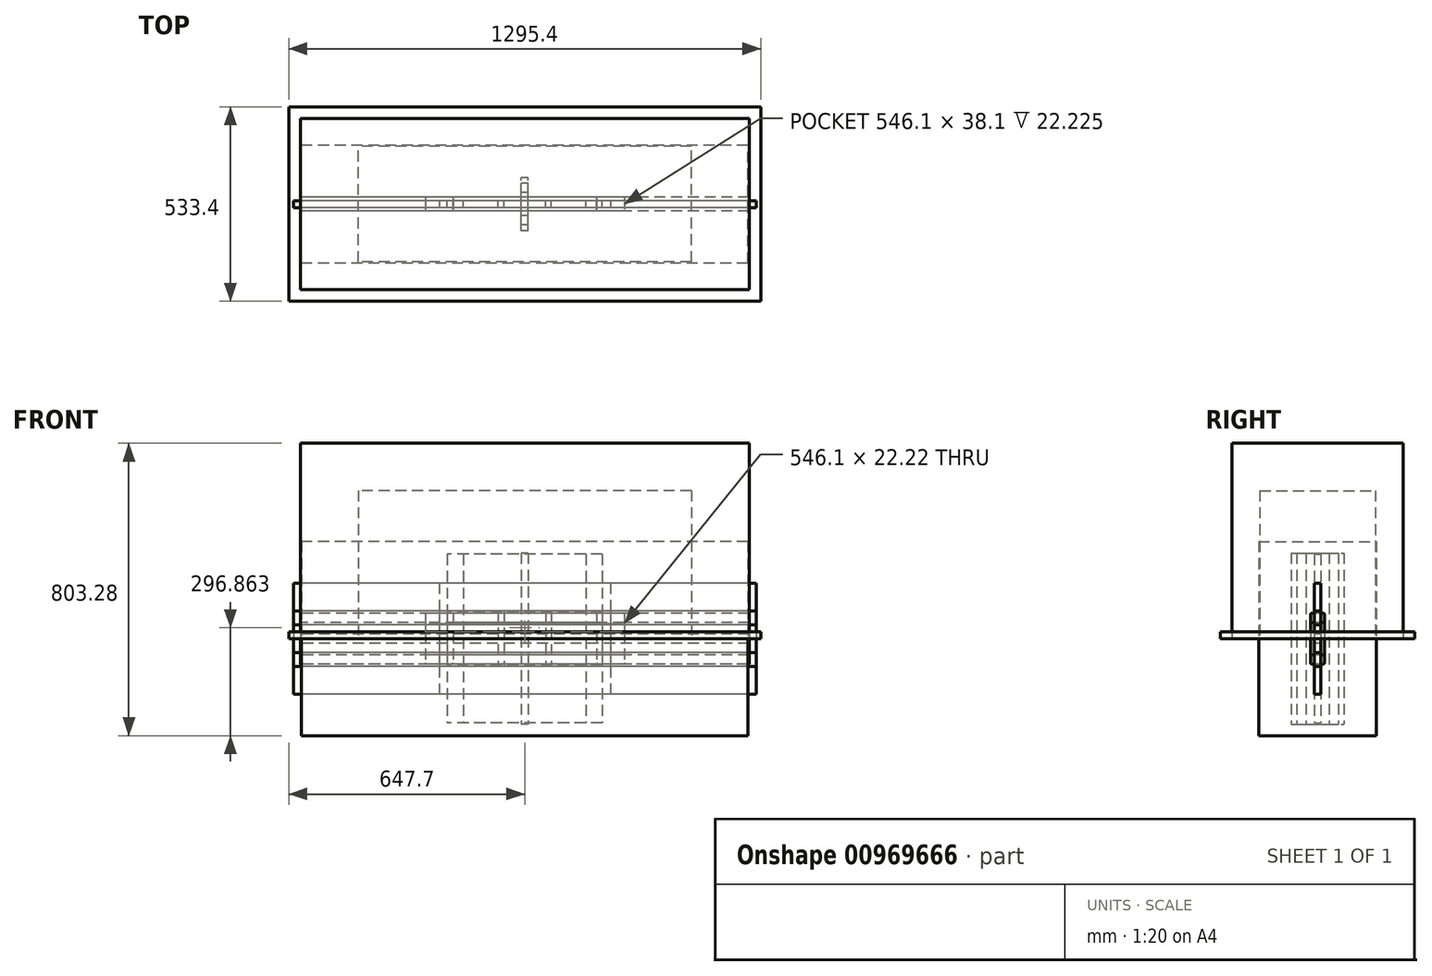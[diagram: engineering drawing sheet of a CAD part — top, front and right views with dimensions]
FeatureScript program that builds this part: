
annotation { "Feature Type Name" : "Feature", "Feature Type Description" : "" }
export const myFeature = defineFeature(function(context is Context, id is Id, definition is map)
    precondition{}
    {
        {
            assignVariable(context, id + "F0", {"name" : "TankLength", "anyValue" : 1231.9 * mm});
        }
        {
            assignVariable(context, id + "F1", {"name" : "TankHeight", "anyValue" : 536.57 * mm});
        }
        {
            assignVariable(context, id + "F2", {"name" : "TankWidth", "anyValue" : 469.9 * mm});
        }
        {
            assignVariable(context, id + "F3", {"name" : "SumpHeight", "lengthValue" : 406.4 * mm, "variableType" : VariableType.LENGTH});
        }
        {
            var Q0;
            Q0=qCreatedBy(makeId("Top.planeOp"),FACE);
            var sketch = newSketch(context, id + "F4", { "sketchPlane" : qUnion([Q0])});
            skLineSegment(sketch, "E0.bottom", {"start": v(615.95, 234.95) * mm, "end": v(-615.95, 234.95) * mm});
            skLineSegment(sketch, "E0.top", {"start": v(615.95, -234.95) * mm, "end": v(-615.95, -234.95) * mm});
            skLineSegment(sketch, "E0.left", {"start": v(615.95, 234.95) * mm, "end": v(615.95, -234.95) * mm});
            skLineSegment(sketch, "E0.right", {"start": v(-615.95, 234.95) * mm, "end": v(-615.95, -234.95) * mm});
            skPoint(sketch, "E0.middle", {"position": v(0, 0) * mm});
            skSolve(sketch);
        }
        {
            var Q0;
            Q0 = qSketchRegion(id + "F4", true);
            extrude(context, id + "F5", {"entities" : qUnion([Q0]), "depth" : getVariable(context, 'TankHeight'), "offsetDistance" : 25.4 * mm});
        }
        {
            var Q0;
            Q0=qCreatedBy(makeId("Top.planeOp"),FACE);
            var sketch = newSketch(context, id + "F6", { "sketchPlane" : qUnion([Q0])});
            skLineSegment(sketch, "E1.bottom", {"start": v(457.2, -158.75) * mm, "end": v(-457.2, -158.75) * mm});
            skLineSegment(sketch, "E1.top", {"start": v(457.2, 158.75) * mm, "end": v(-457.2, 158.75) * mm});
            skLineSegment(sketch, "E1.left", {"start": v(457.2, -158.75) * mm, "end": v(457.2, 158.75) * mm});
            skLineSegment(sketch, "E1.right", {"start": v(-457.2, -158.75) * mm, "end": v(-457.2, 158.75) * mm});
            skPoint(sketch, "E1.middle", {"position": v(0, 0) * mm});
            skSolve(sketch);
        }
        {
            var Q0;
            Q0 = qSketchRegion(id + "F6", true);
            extrude(context, id + "F7", {"entities" : qUnion([Q0]), "depth" : (getVariable(context, 'SumpHeight')), "offsetDistance" : 25.4 * mm});
        }
        {
            assignVariable(context, id + "F8", {"variableType" : VariableType.LENGTH, "name" : "PlywoodThickness", "lengthValue" : 19.05 * mm});
        }
        {
            var Q0;
            Q0=qCreatedBy(makeId("Top.planeOp"),FACE);
            var sketch = newSketch(context, id + "F9", { "sketchPlane" : qUnion([Q0])});
            skLineSegment(sketch, "E2.0", {"start": v(647.7, -266.7) * mm, "end": v(-647.7, -266.7) * mm});
            skLineSegment(sketch, "E2.1", {"start": v(647.7, 266.7) * mm, "end": v(647.7, -266.7) * mm});
            skLineSegment(sketch, "E2.2", {"start": v(-647.7, 266.7) * mm, "end": v(647.7, 266.7) * mm});
            skLineSegment(sketch, "E2.3", {"start": v(-647.7, -266.7) * mm, "end": v(-647.7, 266.7) * mm});
            skSolve(sketch);
        }
        {
            var Q0;
            Q0 = qSketchRegion(id + "F9", true);
            extrude(context, id + "F10", {"entities" : qUnion([Q0]), "depth" : getVariable(context, 'PlywoodThickness'), "offsetDistance" : 25.4 * mm});
        }
        {
            var Q0;
            Q0=qCreatedBy(makeId("Right.planeOp"),FACE);
            var sketch = newSketch(context, id + "F11", { "sketchPlane" : qUnion([Q0])});
            skLineSegment(sketch, "E3.bottom", {"start": v(15.88, 44.45) * mm, "end": v(-15.87, 44.45) * mm});
            skLineSegment(sketch, "E3.top", {"start": v(15.88, -44.45) * mm, "end": v(-15.88, -44.45) * mm});
            skLineSegment(sketch, "E3.left", {"start": v(19.05, 41.28) * mm, "end": v(19.05, -41.28) * mm});
            skLineSegment(sketch, "E3.right", {"start": v(-19.05, 41.28) * mm, "end": v(-19.05, -41.28) * mm});
            skPoint(sketch, "E3.middle", {"position": v(0, 0) * mm});
            skPoint(sketch, "E4.visualSharp", {"position": v(-19.05, 44.45) * mm});
            skArc(sketch, "E4.filletArc", {"start": v(-15.87, 44.45) * mm, "mid": v(-18.12, 43.52) * mm, "end": v(-19.05, 41.28) * mm});
            skPoint(sketch, "E5.visualSharp", {"position": v(19.05, 44.45) * mm});
            skArc(sketch, "E5.filletArc", {"start": v(19.05, 41.28) * mm, "mid": v(18.12, 43.52) * mm, "end": v(15.88, 44.45) * mm});
            skPoint(sketch, "E6.visualSharp", {"position": v(19.05, -44.45) * mm});
            skArc(sketch, "E6.filletArc", {"start": v(15.88, -44.45) * mm, "mid": v(18.12, -43.52) * mm, "end": v(19.05, -41.28) * mm});
            skPoint(sketch, "E7.visualSharp", {"position": v(-19.05, -44.45) * mm});
            skArc(sketch, "E7.filletArc", {"start": v(-19.05, -41.28) * mm, "mid": v(-18.12, -43.52) * mm, "end": v(-15.88, -44.45) * mm});
            skSolve(sketch);
        }
        {
            var Q0;
            Q0=qCreatedBy(makeId("Right.planeOp"),FACE);
            var sketch = newSketch(context, id + "F12", { "sketchPlane" : qUnion([Q0])});
            skLineSegment(sketch, "E8.bottom", {"start": v(15.88, 69.85) * mm, "end": v(-15.87, 69.85) * mm});
            skLineSegment(sketch, "E8.top", {"start": v(15.88, -69.85) * mm, "end": v(-15.87, -69.85) * mm});
            skLineSegment(sketch, "E8.left", {"start": v(19.05, 66.67) * mm, "end": v(19.05, -66.68) * mm});
            skLineSegment(sketch, "E8.right", {"start": v(-19.05, 66.67) * mm, "end": v(-19.05, -66.68) * mm});
            skPoint(sketch, "E8.middle", {"position": v(0, 0) * mm});
            skPoint(sketch, "E9.visualSharp", {"position": v(-19.05, 69.85) * mm});
            skArc(sketch, "E9.filletArc", {"start": v(-15.87, 69.85) * mm, "mid": v(-18.12, 68.92) * mm, "end": v(-19.05, 66.67) * mm});
            skPoint(sketch, "E10.visualSharp", {"position": v(19.05, 69.85) * mm});
            skArc(sketch, "E10.filletArc", {"start": v(19.05, 66.67) * mm, "mid": v(18.12, 68.92) * mm, "end": v(15.88, 69.85) * mm});
            skPoint(sketch, "E11.visualSharp", {"position": v(19.05, -69.85) * mm});
            skArc(sketch, "E11.filletArc", {"start": v(15.88, -69.85) * mm, "mid": v(18.12, -68.92) * mm, "end": v(19.05, -66.68) * mm});
            skPoint(sketch, "E12.visualSharp", {"position": v(-19.05, -69.85) * mm});
            skArc(sketch, "E12.filletArc", {"start": v(-19.05, -66.68) * mm, "mid": v(-18.12, -68.92) * mm, "end": v(-15.87, -69.85) * mm});
            skSolve(sketch);
        }
        {
            var Q0;
            Q0 = qSketchRegion(id + "F12", true);
            extrude(context, id + "F13", {"entities" : qUnion([Q0]), "endBound" : BoundingType.SYMMETRIC, "depth" : getVariable(context, 'TankWidth') - 76.2 * mm, "offsetDistance" : 25.4 * mm});
        }
        {
            var Q0;
            Q0 = qSketchRegion(id + "F12", true);
            extrude(context, id + "F14", {"entities" : qUnion([Q0]), "endBound" : BoundingType.SYMMETRIC, "depth" : getVariable(context, 'TankLength'), "offsetDistance" : 25.4 * mm});
        }
        {
            var Q0;
            Q0 = qSketchRegion(id + "F11", true);
            extrude(context, id + "F15", {"entities" : qUnion([Q0]), "endBound" : BoundingType.SYMMETRIC, "depth" : getVariable(context, 'TankWidth') - 76.2 * mm, "offsetDistance" : 25.4 * mm});
        }
        {
            var Q0;
            Q0 = qSketchRegion(id + "F11", true);
            extrude(context, id + "F16", {"entities" : qUnion([Q0]), "endBound" : BoundingType.SYMMETRIC, "depth" : getVariable(context, 'TankLength'), "offsetDistance" : 25.4 * mm});
        }
        {
            assignVariable(context, id + "F17", {"variableType" : VariableType.LENGTH, "name" : "StandHeight", "lengthValue" : 812.8 * mm});
        }
        {
            var Q0;
            Q0 = qSketchRegion(id + "F12", true);
            extrude(context, id + "F18", {"entities" : qUnion([Q0]), "endBound" : BoundingType.SYMMETRIC, "depth" : getVariable(context, 'StandHeight') - 88.9 * mm - 139.7 * mm - (getVariable(context, 'PlywoodThickness') * 2), "offsetDistance" : 25.4 * mm});
        }
        {
            var Q0;
            Q0 = qSketchRegion(id + "F11", true);
            extrude(context, id + "F19", {"entities" : qUnion([Q0]), "endBound" : BoundingType.SYMMETRIC, "depth" : getVariable(context, 'StandHeight') - 88.9 * mm - 139.7 * mm - (getVariable(context, 'PlywoodThickness') * 2), "offsetDistance" : 25.4 * mm});
        }
        {
            var Q0;
            Q0 = qSketchRegion(id + "F11", true);
            extrude(context, id + "F20", {"entities" : qUnion([Q0]), "endBound" : BoundingType.SYMMETRIC, "depth" : getVariable(context, 'StandHeight') - 88.9 * mm - 139.7 * mm - (getVariable(context, 'PlywoodThickness') * 2), "offsetDistance" : 25.4 * mm});
        }
        {
            var Q0;
            Q0=makeQuery(id+"F20.opExtrude","CAP_FACE",FACE,{"disambiguationData":[OSD([sQuery(id+"F11.wireOp",EDGE,"E3.bottom"),sQuery(id+"F11.wireOp",EDGE,"E3.top"),sQuery(id+"F11.wireOp",EDGE,"E3.left"),sQuery(id+"F11.wireOp",EDGE,"E3.right"),sQuery(id+"F11.wireOp",EDGE,"E4.filletArc"),sQuery(id+"F11.wireOp",EDGE,"E5.filletArc"),sQuery(id+"F11.wireOp",EDGE,"E6.filletArc"),sQuery(id+"F11.wireOp",EDGE,"E7.filletArc")])],"isStart":true});
            var sketch = newSketch(context, id + "F21", { "sketchPlane" : qUnion([Q0])});
            skLineSegment(sketch, "E13", {"start": v(-19.05, 19.05) * mm, "end": v(19.05, 19.05) * mm});
            skSolve(sketch);
        }
        {
            var Q0;
            {var subQ2=sQuery(id+"F21.wireOp",EDGE,"E13");Q0=makeQuery(id+"F21.imprint","IMPRINT",FACE,{"disambiguationData":[TD([[makeQuery(id+"F21.imprint","IMPRINT",EDGE,{"derivedFrom":subQ2}),1.0]])]});}
            var Q1;
            Q1=makeQuery(id+"F20.opExtrude","CAP_FACE",FACE,{"disambiguationData":[OSD([sQuery(id+"F11.wireOp",EDGE,"E3.bottom"),sQuery(id+"F11.wireOp",EDGE,"E3.top"),sQuery(id+"F11.wireOp",EDGE,"E3.left"),sQuery(id+"F11.wireOp",EDGE,"E3.right"),sQuery(id+"F11.wireOp",EDGE,"E4.filletArc"),sQuery(id+"F11.wireOp",EDGE,"E5.filletArc"),sQuery(id+"F11.wireOp",EDGE,"E6.filletArc"),sQuery(id+"F11.wireOp",EDGE,"E7.filletArc")])],"isStart":false});
            extrude(context, id + "F22", {"entities" : qUnion([Q0]), "operationType" : NewBodyOperationType.REMOVE, "endBound" : BoundingType.UP_TO_SURFACE, "oppositeDirection" : true, "depth" : 25.4 * mm, "endBoundEntityFace" : qUnion([Q1]), "offsetDistance" : 25.4 * mm});
        }
        {
            var Q0;
            Q0=qCreatedBy(makeId("Right.planeOp"),FACE);
            var sketch = newSketch(context, id + "F23", { "sketchPlane" : qUnion([Q0])});
            skLineSegment(sketch, "E14.bottom", {"start": v(9.52, 76.2) * mm, "end": v(-9.52, 76.2) * mm});
            skLineSegment(sketch, "E14.top", {"start": v(9.52, -76.2) * mm, "end": v(-9.52, -76.2) * mm});
            skLineSegment(sketch, "E14.left", {"start": v(9.52, 76.2) * mm, "end": v(9.52, -76.2) * mm});
            skLineSegment(sketch, "E14.right", {"start": v(-9.52, 76.2) * mm, "end": v(-9.52, -76.2) * mm});
            skPoint(sketch, "E14.middle", {"position": v(0, 0) * mm});
            skSolve(sketch);
        }
        {
            var Q0;
            Q0 = qSketchRegion(id + "F23", true);
            extrude(context, id + "F24", {"entities" : qUnion([Q0]), "endBound" : BoundingType.SYMMETRIC, "depth" : getVariable(context, 'TankWidth'), "offsetDistance" : 25.4 * mm});
        }
        {
            var Q0;
            Q0 = qSketchRegion(id + "F23", true);
            extrude(context, id + "F25", {"entities" : qUnion([Q0]), "endBound" : BoundingType.SYMMETRIC, "depth" : getVariable(context, 'TankLength') + (getVariable(context, 'PlywoodThickness') * 2), "offsetDistance" : 25.4 * mm});
        }
        {
            assignVariable(context, id + "F26", {"variableType" : VariableType.LENGTH, "name" : "SideVerticalStripWidth", "lengthValue" : 63.5 * mm});
        }
        {
            var Q0;
            Q0=qCreatedBy(makeId("Front.planeOp"),FACE);
            var sketch = newSketch(context, id + "F27", { "sketchPlane" : qUnion([Q0])});
            skLineSegment(sketch, "E15.bottom", {"start": v(9.53, 234.95) * mm, "end": v(-9.53, 234.95) * mm});
            skLineSegment(sketch, "E15.top", {"start": v(9.53, -234.95) * mm, "end": v(-9.53, -234.95) * mm});
            skLineSegment(sketch, "E15.left", {"start": v(9.53, 234.95) * mm, "end": v(9.53, -234.95) * mm});
            skLineSegment(sketch, "E15.right", {"start": v(-9.53, 234.95) * mm, "end": v(-9.53, -234.95) * mm});
            skPoint(sketch, "E15.middle", {"position": v(0, 0) * mm});
            skSolve(sketch);
        }
        {
            var Q0;
            Q0 = qSketchRegion(id + "F27", true);
            extrude(context, id + "F28", {"entities" : qUnion([Q0]), "endBound" : BoundingType.SYMMETRIC, "depth" : getVariable(context, 'SideVerticalStripWidth'), "offsetDistance" : 25.4 * mm});
        }
        {
            var Q0;
            Q0 = qSketchRegion(id + "F27", true);
            extrude(context, id + "F29", {"entities" : qUnion([Q0]), "endBound" : BoundingType.SYMMETRIC, "depth" : getVariable(context, 'PlywoodThickness') + 38.1 * mm + 88.9 * mm, "offsetDistance" : 25.4 * mm});
        }
        {
            assignVariable(context, id + "F30", {"variableType" : VariableType.LENGTH, "name" : "DoorCenterOverlap", "lengthValue" : 12.7 * mm});
        }
        {
            var Q0;
            Q0 = qSketchRegion(id + "F27", true);
            extrude(context, id + "F31", {"entities" : qUnion([Q0]), "endBound" : BoundingType.SYMMETRIC, "depth" : 139.7 * mm - (getVariable(context, 'DoorCenterOverlap') * 2), "offsetDistance" : 25.4 * mm});
        }
        {
            var Q0;
            Q0=qCreatedBy(makeId("Front.planeOp"),FACE);
            var sketch = newSketch(context, id + "F32", { "sketchPlane" : qUnion([Q0])});
            skLineSegment(sketch, "E16.bottom", {"start": v(212.72, 231.78) * mm, "end": v(-212.73, 231.78) * mm});
            skLineSegment(sketch, "E16.top", {"start": v(212.73, -231.78) * mm, "end": v(-212.72, -231.78) * mm});
            skLineSegment(sketch, "E16.left", {"start": v(212.72, 231.78) * mm, "end": v(212.73, -231.78) * mm});
            skLineSegment(sketch, "E16.right", {"start": v(-212.73, 231.78) * mm, "end": v(-212.72, -231.78) * mm});
            skPoint(sketch, "E16.middle", {"position": v(0, 0) * mm});
            skSolve(sketch);
        }
        {
            var Q0;
            Q0 = qSketchRegion(id + "F32", true);
            extrude(context, id + "F33", {"entities" : qUnion([Q0]), "endBound" : BoundingType.SYMMETRIC, "depth" : getVariable(context, 'PlywoodThickness'), "offsetDistance" : 25.4 * mm});
        }
        {
            var Q0;
            Q0=qCreatedBy(makeId("Front.planeOp"),FACE);
            var sketch = newSketch(context, id + "F34", { "sketchPlane" : qUnion([Q0])});
            skLineSegment(sketch, "E17.bottom", {"start": v(168.27, 231.78) * mm, "end": v(-168.28, 231.78) * mm});
            skLineSegment(sketch, "E17.top", {"start": v(168.28, -231.78) * mm, "end": v(-168.27, -231.78) * mm});
            skLineSegment(sketch, "E17.left", {"start": v(168.27, 231.78) * mm, "end": v(168.28, -231.78) * mm});
            skLineSegment(sketch, "E17.right", {"start": v(-168.28, 231.78) * mm, "end": v(-168.27, -231.78) * mm});
            skPoint(sketch, "E17.middle", {"position": v(0, 0) * mm});
            skSolve(sketch);
        }
        {
            var Q0;
            Q0 = qSketchRegion(id + "F34", true);
            extrude(context, id + "F35", {"entities" : qUnion([Q0]), "endBound" : BoundingType.SYMMETRIC, "depth" : getVariable(context, 'PlywoodThickness'), "offsetDistance" : 25.4 * mm});
        }
        {
            assignVariable(context, id + "F36", {"variableType" : VariableType.LENGTH, "name" : "CurrentTankWidth", "lengthValue" : 323.85 * mm});
        }
        {
            var Q0;
            Q0=qCreatedBy(makeId("Front.planeOp"),FACE);
            var sketch = newSketch(context, id + "F37", { "sketchPlane" : qUnion([Q0])});
            skLineSegment(sketch, "E18.bottom", {"start": v(612.78, 266.7) * mm, "end": v(-612.78, 266.7) * mm});
            skLineSegment(sketch, "E18.top", {"start": v(612.78, -266.7) * mm, "end": v(-612.78, -266.7) * mm});
            skLineSegment(sketch, "E18.left", {"start": v(612.78, 266.7) * mm, "end": v(612.78, -266.7) * mm});
            skLineSegment(sketch, "E18.right", {"start": v(-612.78, 266.7) * mm, "end": v(-612.78, -266.7) * mm});
            skPoint(sketch, "E18.middle", {"position": v(0, 0) * mm});
            skSolve(sketch);
        }
        {
            var Q0;
            Q0 = qSketchRegion(id + "F37", true);
            extrude(context, id + "F38", {"entities" : qUnion([Q0]), "endBound" : BoundingType.SYMMETRIC, "depth" : getVariable(context, 'CurrentTankWidth'), "offsetDistance" : 25.4 * mm});
        }
        {
            var Q0;
            Q0=qCreatedBy(makeId("Right.planeOp"),FACE);
            var sketch = newSketch(context, id + "F39", { "sketchPlane" : qUnion([Q0])});
            skLineSegment(sketch, "E19.bottom", {"start": v(9.53, 152.4) * mm, "end": v(-9.52, 152.4) * mm});
            skLineSegment(sketch, "E19.top", {"start": v(9.53, -152.4) * mm, "end": v(-9.53, -152.4) * mm});
            skLineSegment(sketch, "E19.left", {"start": v(9.53, 152.4) * mm, "end": v(9.53, -152.4) * mm});
            skLineSegment(sketch, "E19.right", {"start": v(-9.52, 152.4) * mm, "end": v(-9.53, -152.4) * mm});
            skPoint(sketch, "E19.middle", {"position": v(0, 0) * mm});
            skSolve(sketch);
        }
        {
            var Q0;
            Q0 = qSketchRegion(id + "F39", true);
            extrude(context, id + "F40", {"entities" : qUnion([Q0]), "endBound" : BoundingType.SYMMETRIC, "depth" : getVariable(context, 'TankWidth'), "offsetDistance" : 25.4 * mm});
        }
        {
            var Q0;
            Q0=qCreatedBy(makeId("Right.planeOp"),FACE);
            var sketch = newSketch(context, id + "F41", { "sketchPlane" : qUnion([Q0])});
            skLineSegment(sketch, "E20.bottom", {"start": v(9.53, 38.1) * mm, "end": v(-9.53, 38.1) * mm});
            skLineSegment(sketch, "E20.top", {"start": v(9.52, -38.1) * mm, "end": v(-9.53, -38.1) * mm});
            skLineSegment(sketch, "E20.left", {"start": v(9.53, 38.1) * mm, "end": v(9.52, -38.1) * mm});
            skLineSegment(sketch, "E20.right", {"start": v(-9.53, 38.1) * mm, "end": v(-9.53, -38.1) * mm});
            skPoint(sketch, "E20.middle", {"position": v(0, 0) * mm});
            skSolve(sketch);
        }
        {
            var Q0;
            Q0 = qSketchRegion(id + "F41", true);
            extrude(context, id + "F42", {"entities" : qUnion([Q0]), "endBound" : BoundingType.SYMMETRIC, "depth" : getVariable(context, 'TankLength') + (2 * getVariable(context, 'PlywoodThickness')), "offsetDistance" : 25.4 * mm});
        }
        {
            var Q0;
            Q0 = qSketchRegion(id + "F39", true);
            extrude(context, id + "F43", {"entities" : qUnion([Q0]), "endBound" : BoundingType.SYMMETRIC, "depth" : getVariable(context, 'TankLength') + (2 * getVariable(context, 'PlywoodThickness')), "offsetDistance" : 25.4 * mm});
        }
        {
            var Q0;
            Q0=qCreatedBy(makeId("Front.planeOp"),FACE);
            var sketch = newSketch(context, id + "F44", { "sketchPlane" : qUnion([Q0])});
            skLineSegment(sketch, "E21.bottom", {"start": v(57.15, 76.2) * mm, "end": v(-57.15, 76.2) * mm});
            skLineSegment(sketch, "E21.top", {"start": v(57.15, -76.2) * mm, "end": v(-57.15, -76.2) * mm});
            skLineSegment(sketch, "E21.left", {"start": v(57.15, 76.2) * mm, "end": v(57.15, -76.2) * mm});
            skLineSegment(sketch, "E21.right", {"start": v(-57.15, 76.2) * mm, "end": v(-57.15, -76.2) * mm});
            skPoint(sketch, "E21.middle", {"position": v(0, 0) * mm});
            skSolve(sketch);
        }
        {
            var Q0;
            Q0 = qSketchRegion(id + "F44", true);
            extrude(context, id + "F45", {"entities" : qUnion([Q0]), "endBound" : BoundingType.SYMMETRIC, "depth" : getVariable(context, 'PlywoodThickness'), "offsetDistance" : 25.4 * mm});
        }
        {
            var Q0;
            Q0=qCreatedBy(makeId("Front.planeOp"),FACE);
            var sketch = newSketch(context, id + "F46", { "sketchPlane" : qUnion([Q0])});
            skLineSegment(sketch, "E22.bottom", {"start": v(73.03, 76.2) * mm, "end": v(-73.03, 76.2) * mm});
            skLineSegment(sketch, "E22.top", {"start": v(73.03, -76.2) * mm, "end": v(-73.03, -76.2) * mm});
            skLineSegment(sketch, "E22.left", {"start": v(73.03, 76.2) * mm, "end": v(73.03, -76.2) * mm});
            skLineSegment(sketch, "E22.right", {"start": v(-73.03, 76.2) * mm, "end": v(-73.03, -76.2) * mm});
            skPoint(sketch, "E22.middle", {"position": v(0, 0) * mm});
            skSolve(sketch);
        }
        {
            var Q0;
            Q0 = qSketchRegion(id + "F46", true);
            extrude(context, id + "F47", {"entities" : qUnion([Q0]), "endBound" : BoundingType.SYMMETRIC, "depth" : getVariable(context, 'PlywoodThickness'), "offsetDistance" : 25.4 * mm});
        }
        {
            var Q0;
            Q0=qCreatedBy(makeId("Front.planeOp"),FACE);
            var sketch = newSketch(context, id + "F48", { "sketchPlane" : qUnion([Q0])});
            skLineSegment(sketch, "E23.bottom", {"start": v(212.73, 73.03) * mm, "end": v(-212.73, 73.03) * mm});
            skLineSegment(sketch, "E23.top", {"start": v(212.73, -73.02) * mm, "end": v(-212.73, -73.02) * mm});
            skLineSegment(sketch, "E23.left", {"start": v(212.73, 73.03) * mm, "end": v(212.73, -73.02) * mm});
            skLineSegment(sketch, "E23.right", {"start": v(-212.73, 73.03) * mm, "end": v(-212.73, -73.02) * mm});
            skPoint(sketch, "E23.middle", {"position": v(0, 0) * mm});
            skSolve(sketch);
        }
        {
            var Q0;
            Q0 = qSketchRegion(id + "F48", true);
            extrude(context, id + "F49", {"entities" : qUnion([Q0]), "endBound" : BoundingType.SYMMETRIC, "depth" : getVariable(context, 'PlywoodThickness'), "offsetDistance" : 25.4 * mm});
        }
        {
            var Q0;
            Q0=qCreatedBy(makeId("Right.planeOp"),FACE);
            var sketch = newSketch(context, id + "F50", { "sketchPlane" : qUnion([Q0])});
            skLineSegment(sketch, "E24.bottom", {"start": v(9.52, 12.7) * mm, "end": v(-9.53, 12.7) * mm});
            skLineSegment(sketch, "E24.top", {"start": v(9.52, -12.7) * mm, "end": v(-9.53, -12.7) * mm});
            skLineSegment(sketch, "E24.left", {"start": v(9.52, 12.7) * mm, "end": v(9.52, -12.7) * mm});
            skLineSegment(sketch, "E24.right", {"start": v(-9.53, 12.7) * mm, "end": v(-9.53, -12.7) * mm});
            skPoint(sketch, "E24.middle", {"position": v(0, 0) * mm});
            skSolve(sketch);
        }
        {
            var Q0;
            Q0 = qSketchRegion(id + "F50", true);
            extrude(context, id + "F51", {"entities" : qUnion([Q0]), "endBound" : BoundingType.SYMMETRIC, "depth" : getVariable(context, 'TankLength'), "offsetDistance" : 25.4 * mm});
        }
    });
